# Revit family: Hager-Univers-IP44-sistema-Montagem_embutida-NoHosted-PT-pt
name_source: partatom
category: Electrical Equipment
units: mm (PartAtom-declared; Revit-internal decimal feet)

## family parameters
Always vertical = Yes
Cut with Voids When Loaded = No
Panel Configuration = Two Columns, Circuits Across
Part Type = Panelboard
Room Calculation Point = No
Round Connector Dimension = Use Diameter
Shared = No
Work Plane-Based = Yes

## types (31) — shared parameters
Default Elevation = 1219 mm
EF000003 - Método de montagem = EV001247 - Montagem em superfície/montagem embutida
EF000007 - Cor = EV000202 - Branco
EF000049 - Profundidade = 161 mm  [stored 0.528215 ft]
EF000116 - Número RAL = 9010
EF000118 - Com tampa de montagem = No
EF000218 - Profundidade incorporada = 161 mm  [stored 0.528215 ft]
EF000339 - Tipo de difusor = EV004216 - Porta
EF001062 - Versão EMC = No
EF001088 - Extensão possível = Yes
EF001134 - Calha DIN = Yes
EF001596 - Material do corpo = EV000179 - Aço
EF002950 - Largura em número de módulos = 12
EF004462 - Tipo de fecho = EV000154 - Outro
EF005474 - Grau de proteção (IP) = EV006418 - IP44
EF006244 - Tampa/porta transparente = No
EF006306 - Com fecho = No
EF015941 - Porta para passagem de sinal = No
HG000002 - Com porta ou tampa = Yes
HG000003 - Gama = Univers
HG000005 - Espessura = 3 mm  [stored 0.00984252 ft]
HG000006 - Encastrado = Yes
HG000011 - Filas vazias desde da parte de baixo = No
HG000017 - Distância entre polos = 18 mm  [stored 0.0590551 ft]
Manufacturer = Hager
Type Comments = Univers
zero-valued in all types: HG000007 - Número de colunas vazias

## per-type parameters (varying)
| type | EF000008 - Largura | EF000040 - Altura | EF000266 - Número de linhas | EF000332 - Altura embutida | EF000846 - Largura para embutir | EF001131 - Profundidade interior | EF009212 - Tipo de tampa | EF015776 - Borne de terra | EF015777 - Borne de neutro | HG000001 - Número de colunas | HG000004 - Referência do Fabricante | HG000008 - Número de filas vazias | HG000009 - Porta dupla | HG000010 - Portas assimétricas | Model |
| Montagem embutida IP44 L1050 A1100 P161 12 unidade de divisão - FWB74A | 1050 mm | 1100 mm | 28 | 1100 mm | 1050 mm | 160 mm  [stored 0.524934 ft] | EV000116 - Fechado | No | No | 4 | FWB74A | 0 | Yes | No | FWB74A |
| Montagem embutida IP44 L1050 A1100 P161 12 unidade de divisão - FWB74N | 1050 mm | 1100 mm | 20 | 1100 mm | 1050 mm | 161 mm  [stored 0.528215 ft] | EV009916 - Com recuo | No | No | 4 | FWB74N | 8 | Yes | No | FWB74N |
| Montagem embutida IP44 L1050 A1100 P161 12 unidade de divisão - FWB74S | 1050 mm | 1100 mm | 28 | 1100 mm | 1050 mm | 161 mm  [stored 0.528215 ft] | EV009916 - Com recuo | No | No | 4 | FWB74S | 0 | Yes | No | FWB74S |
| Montagem embutida IP44 L1050 A500 P161 12 unidade de divisão - FWB34S | 1050 mm | 500 mm  [stored 1.64042 ft] | 12 | 500 mm  [stored 1.64042 ft] | 1050 mm | 161 mm  [stored 0.528215 ft] | EV009916 - Com recuo | Yes | Yes | 4 | FWB34S | 0 | Yes | No | FWB34S |
| Montagem embutida IP44 L1050 A650 P161 12 unidade de divisão - FWB44S | 1050 mm | 650 mm  [stored 2.13255 ft] | 16 | 650 mm  [stored 2.13255 ft] | 1050 mm | 161 mm  [stored 0.528215 ft] | EV009916 - Com recuo | Yes | Yes | 4 | FWB44S | 0 | Yes | No | FWB44S |
| Montagem embutida IP44 L1050 A800 P161 12 unidade de divisão - FWB54S | 1050 mm | 800 mm  [stored 2.62467 ft] | 20 | 800 mm  [stored 2.62467 ft] | 1050 mm | 161 mm  [stored 0.528215 ft] | EV009916 - Com recuo | Yes | Yes | 4 | FWB54S | 0 | Yes | No | FWB54S |
| Montagem embutida IP44 L1050 A950 P161 12 unidade de divisão - FWB64N | 1050 mm | 950 mm  [stored 3.1168 ft] | 16 | 950 mm  [stored 3.1168 ft] | 1050 mm | 161 mm  [stored 0.528215 ft] | EV009916 - Com recuo | No | No | 4 | FWB64N | 8 | Yes | No | FWB64N |
| Montagem embutida IP44 L1050 A950 P161 12 unidade de divisão - FWB64S | 1050 mm | 950 mm  [stored 3.1168 ft] | 24 | 950 mm  [stored 3.1168 ft] | 1050 mm | 161 mm  [stored 0.528215 ft] | EV009916 - Com recuo | Yes | Yes | 4 | FWB64S | 0 | Yes | No | FWB64S |
| Montagem embutida IP44 L300 A1100 P161 12 unidade de divisão - FWB71S | 300 mm | 1100 mm | 7 | 1100 mm | 300 mm | 161 mm  [stored 0.528215 ft] | EV009916 - Com recuo | Yes | Yes | 1 | FWB71S | 0 | No | No | FWB71S |
| Montagem embutida IP44 L300 A500 P161 12 unidade de divisão - FWB31S | 300 mm | 500 mm  [stored 1.64042 ft] | 3 | 500 mm  [stored 1.64042 ft] | 300 mm | 161 mm  [stored 0.528215 ft] | EV009916 - Com recuo | Yes | Yes | 1 | FWB31S | 0 | No | No | FWB31S |
| Montagem embutida IP44 L300 A650 P161 12 unidade de divisão - FWB41S | 300 mm | 650 mm  [stored 2.13255 ft] | 4 | 650 mm  [stored 2.13255 ft] | 300 mm | 160 mm  [stored 0.524934 ft] | EV009916 - Com recuo | Yes | Yes | 1 | FWB41S | 0 | No | No | FWB41S |
| Montagem embutida IP44 L300 A800 P161 12 unidade de divisão - FWB51S | 300 mm | 800 mm  [stored 2.62467 ft] | 5 | 800 mm  [stored 2.62467 ft] | 300 mm | 161 mm  [stored 0.528215 ft] | EV009916 - Com recuo | Yes | Yes | 1 | FWB51S | 0 | No | No | FWB51S |
| Montagem embutida IP44 L300 A950 P161 12 unidade de divisão - FWB61S | 300 mm | 950 mm  [stored 3.1168 ft] | 6 | 950 mm  [stored 3.1168 ft] | 300 mm | 161 mm  [stored 0.528215 ft] | EV009916 - Com recuo | Yes | Yes | 1 | FWB61S | 0 | No | No | FWB61S |
| Montagem embutida IP44 L550 A1100 P161 12 unidade de divisão - FWB72N | 550 mm | 1100 mm | 10 | 1100 mm | 550 mm | 161 mm  [stored 0.528215 ft] | EV009916 - Com recuo | No | No | 2 | FWB72N | 4 | No | No | FWB72N |
| Montagem embutida IP44 L550 A1100 P161 12 unidade de divisão - FWB72S | 550 mm | 1100 mm | 14 | 1100 mm | 550 mm | 161 mm  [stored 0.528215 ft] | EV009916 - Com recuo | No | No | 2 | FWB72S | 0 | No | No | FWB72S |
| Montagem embutida IP44 L550 A500 P161 12 unidade de divisão - FWB32S | 550 mm | 500 mm  [stored 1.64042 ft] | 6 | 500 mm  [stored 1.64042 ft] | 550 mm | 161 mm  [stored 0.528215 ft] | EV009916 - Com recuo | Yes | Yes | 2 | FWB32S | 0 | No | No | FWB32S |
| Montagem embutida IP44 L550 A650 P161 12 unidade de divisão - FWB42S | 550 mm | 650 mm  [stored 2.13255 ft] | 8 | 650 mm  [stored 2.13255 ft] | 550 mm | 161 mm  [stored 0.528215 ft] | EV009916 - Com recuo | No | No | 2 | FWB42S | 0 | No | No | FWB42S |
| Montagem embutida IP44 L550 A800 P161 12 unidade de divisão - FWB52N | 550 mm | 800 mm  [stored 2.62467 ft] | 6 | 800 mm  [stored 2.62467 ft] | 550 mm | 161 mm  [stored 0.528215 ft] | EV009916 - Com recuo | No | No | 2 | FWB52N | 4 | No | No | FWB52N |
| Montagem embutida IP44 L550 A800 P161 12 unidade de divisão - FWB52S | 550 mm | 800 mm  [stored 2.62467 ft] | 10 | 800 mm  [stored 2.62467 ft] | 550 mm | 161 mm  [stored 0.528215 ft] |  | Yes | Yes | 2 | FWB52S | 0 | No | No | FWB52S |
| Montagem embutida IP44 L550 A950 P161 12 unidade de divisão - FWB62A | 550 mm | 950 mm  [stored 3.1168 ft] | 12 | 950 mm  [stored 3.1168 ft] | 550 mm | 160 mm  [stored 0.524934 ft] | EV000116 - Fechado | No | No | 2 | FWB62A | 0 | No | No | FWB62A |
| Montagem embutida IP44 L550 A950 P161 12 unidade de divisão - FWB62N | 550 mm | 950 mm  [stored 3.1168 ft] | 8 | 950 mm  [stored 3.1168 ft] | 550 mm | 161 mm  [stored 0.528215 ft] | EV009916 - Com recuo | No | No | 2 | FWB62N | 4 | No | No | FWB62N |
| Montagem embutida IP44 L550 A950 P161 12 unidade de divisão - FWB62S | 550 mm | 950 mm  [stored 3.1168 ft] | 12 | 950 mm  [stored 3.1168 ft] | 550 mm | 160 mm  [stored 0.524934 ft] | EV009916 - Com recuo | Yes | Yes | 2 | FWB62S | 0 | No | No | FWB62S |
| Montagem embutida IP44 L800 A1100 P161 12 unidade de divisão - FWB73N | 800 mm  [stored 2.62467 ft] | 1100 mm | 15 | 1100 mm | 800 mm  [stored 2.62467 ft] | 161 mm  [stored 0.528215 ft] | EV009916 - Com recuo | No | No | 3 | FWB73N | 6 | Yes | Yes | FWB73N |
| Montagem embutida IP44 L800 A1100 P161 12 unidade de divisão - FWB73S | 800 mm  [stored 2.62467 ft] | 1100 mm | 21 | 1100 mm | 800 mm  [stored 2.62467 ft] | 161 mm  [stored 0.528215 ft] | EV009916 - Com recuo | No | No | 3 | FWB73S | 0 | Yes | Yes | FWB73S |
| Montagem embutida IP44 L800 A500 P161 12 unidade de divisão - FWB33S | 800 mm  [stored 2.62467 ft] | 500 mm  [stored 1.64042 ft] | 9 | 500 mm  [stored 1.64042 ft] | 800 mm  [stored 2.62467 ft] | 161 mm  [stored 0.528215 ft] | EV009916 - Com recuo | Yes | Yes | 3 | FWB33S | 0 | Yes | Yes | FWB33S |
| Montagem embutida IP44 L800 A650 P161 12 unidade de divisão - FWB43S | 800 mm  [stored 2.62467 ft] | 650 mm  [stored 2.13255 ft] | 12 | 650 mm  [stored 2.13255 ft] | 800 mm  [stored 2.62467 ft] | 160 mm  [stored 0.524934 ft] | EV009916 - Com recuo | Yes | Yes | 3 | FWB43S | 0 | Yes | Yes | FWB43S |
| Montagem embutida IP44 L800 A800 P161 12 unidade de divisão - FWB53N | 800 mm  [stored 2.62467 ft] | 800 mm  [stored 2.62467 ft] | 9 | 800 mm  [stored 2.62467 ft] | 800 mm  [stored 2.62467 ft] | 161 mm  [stored 0.528215 ft] | EV009916 - Com recuo | No | No | 3 | FWB53N | 6 | Yes | Yes | FWB53N |
| Montagem embutida IP44 L800 A800 P161 12 unidade de divisão - FWB53S | 800 mm  [stored 2.62467 ft] | 800 mm  [stored 2.62467 ft] | 15 | 800 mm  [stored 2.62467 ft] | 800 mm  [stored 2.62467 ft] | 160 mm  [stored 0.524934 ft] | EV009916 - Com recuo | Yes | Yes | 3 | FWB53S | 0 | Yes | Yes | FWB53S |
| Montagem embutida IP44 L800 A950 P161 12 unidade de divisão - FWB63A | 800 mm  [stored 2.62467 ft] | 950 mm  [stored 3.1168 ft] | 18 | 950 mm  [stored 3.1168 ft] | 800 mm  [stored 2.62467 ft] | 160 mm  [stored 0.524934 ft] | EV000116 - Fechado | No | No | 3 | FWB63A | 0 | Yes | Yes | FWB63A |
| Montagem embutida IP44 L800 A950 P161 12 unidade de divisão - FWB63N | 800 mm  [stored 2.62467 ft] | 950 mm  [stored 3.1168 ft] | 12 | 950 mm  [stored 3.1168 ft] | 800 mm  [stored 2.62467 ft] | 161 mm  [stored 0.528215 ft] | EV009916 - Com recuo | No | No | 3 | FWB63N | 6 | Yes | Yes | FWB63N |
| Montagem embutida IP44 L800 A950 P161 12 unidade de divisão - FWB63S | 800 mm  [stored 2.62467 ft] | 950 mm  [stored 3.1168 ft] | 18 | 950 mm  [stored 3.1168 ft] | 800 mm  [stored 2.62467 ft] | 160 mm  [stored 0.524934 ft] | EV009916 - Com recuo | Yes | Yes | 3 | FWB63S | 0 | Yes | Yes | FWB63S |

note: [stored X ft] marks values corroborated as IEEE doubles in the binary element streams (Revit-internal decimal feet)

## geometry (parser evidence)
native form markers: Sweep x13
no freeform markers — native parametric forms only
